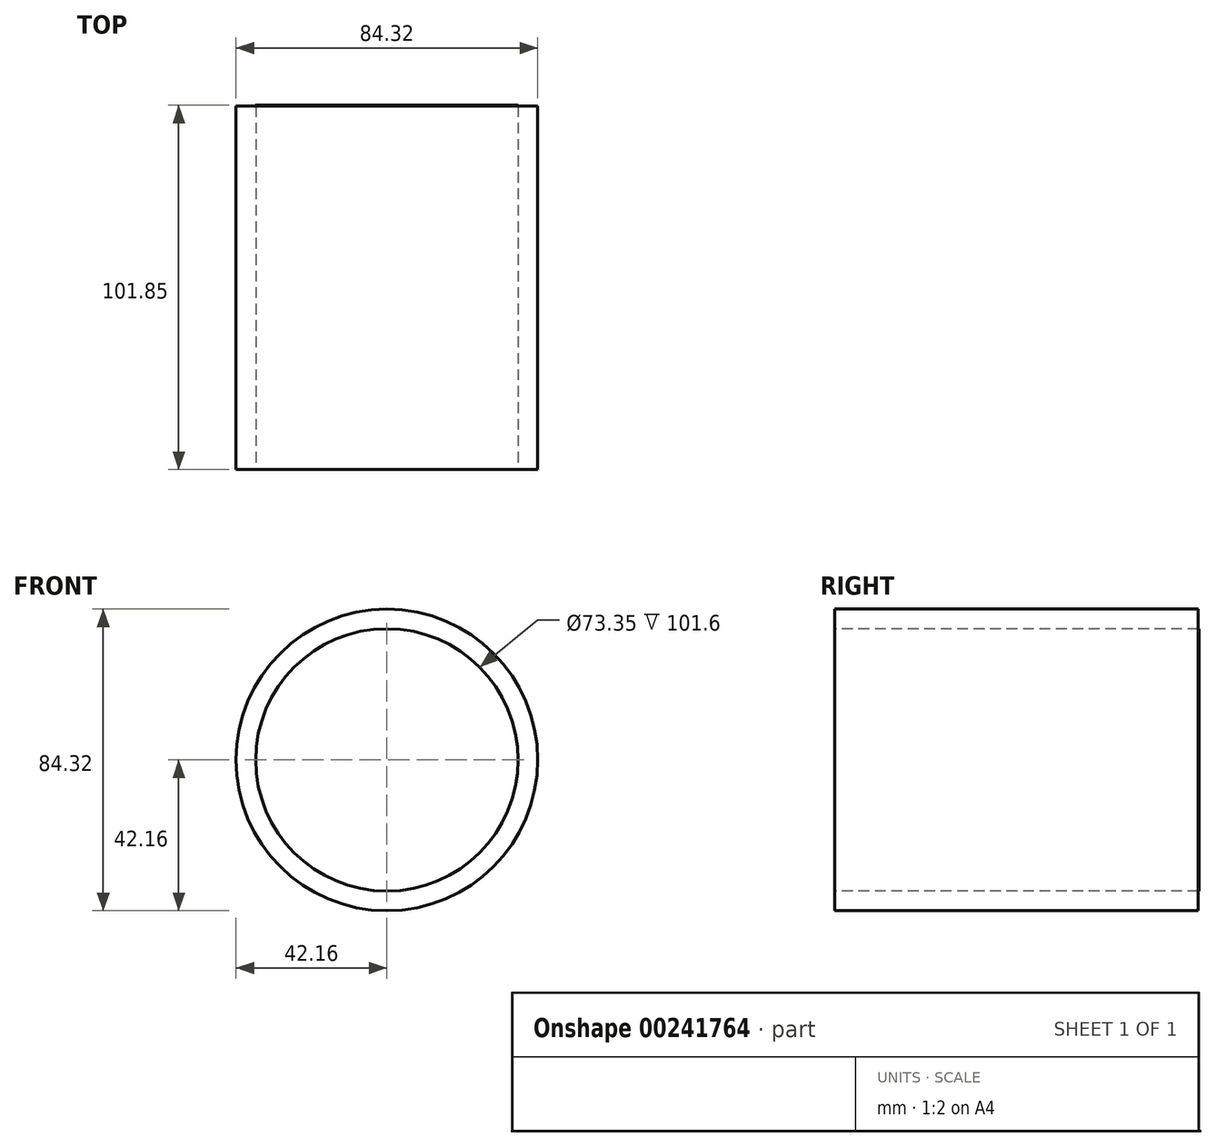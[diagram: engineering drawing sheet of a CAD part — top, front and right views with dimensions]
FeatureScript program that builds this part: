
annotation { "Feature Type Name" : "Feature", "Feature Type Description" : "" }
export const myFeature = defineFeature(function(context is Context, id is Id, definition is map)
    precondition{}
    {
        {
            var Q0;
            Q0=qCreatedBy(makeId("Front.planeOp"),FACE);
            var sketch = newSketch(context, id + "F0", { "sketchPlane" : qUnion([Q0])});
            skCircle(sketch, "E0", {"center": v(0, 0) * mm, "radius": 42.16 * mm});
            skCircle(sketch, "E1", {"center": v(0, 0) * mm, "radius": 36.67 * mm});
            skSolve(sketch);
        }
        {
            var Q0;
            Q0 = qSketchRegion(id + "F0", true);
            extrude(context, id + "F1", {"entities" : qUnion([Q0]), "oppositeDirection" : true, "depth" : 101.6 * mm});
        }
        {
            var Q0;
            Q0=makeQuery(id+"F1.opExtrude","CAP_FACE",FACE,{"disambiguationData":[OSD([sQuery(id+"F0.wireOp",EDGE,"E0"),sQuery(id+"F0.wireOp",EDGE,"E1")])],"isStart":false});
            var sketch = newSketch(context, id + "F2", { "sketchPlane" : qUnion([Q0])});
            skCircle(sketch, "E2", {"center": v(0, 0) * mm, "radius": 36.7 * mm});
            skSolve(sketch);
        }
        {
            var Q0;
            Q0 = qSketchRegion(id + "F2", true);
            extrude(context, id + "F3", {"entities" : qUnion([Q0]), "operationType" : NewBodyOperationType.ADD, "depth" : 0.25 * mm});
        }
        {
            var Q0;
            Q0=qCreatedBy(makeId("Right.planeOp"),FACE);
            var sketch = newSketch(context, id + "F4", { "sketchPlane" : qUnion([Q0])});
            skFitSpline(sketch, "E3", {"points": [v(2.39, -43.99) * mm, v(16.51, -67.5) * mm, v(52.53, -70.14) * mm, v(88.1, -66.72) * mm, v(94.18, -46.25) * mm], "startDerivative": vector(42.71, -120.41) * mm, "endDerivative": vector(6.17, 116.7) * mm});
            skFitSpline(sketch, "E4", {"points": [v(94.18, -46.25) * mm, v(94.18, -41.57) * mm], "startDerivative": vector(0, 4.69) * mm, "endDerivative": vector(0, 4.69) * mm});
            skFitSpline(sketch, "E5", {"points": [v(2.39, -43.99) * mm, v(2.39, -41.39) * mm], "startDerivative": vector(0, 2.6) * mm, "endDerivative": vector(0, 2.6) * mm});
            skFitSpline(sketch, "E6", {"points": [v(5.8, -43.99) * mm, v(18.26, -61.98) * mm, v(54.3, -63.38) * mm, v(81, -60.87) * mm, v(84.85, -53.6) * mm, v(85.79, -41.6) * mm], "startDerivative": vector(41.98, -104.35) * mm, "endDerivative": vector(3.32, 80.13) * mm});
            skSolve(sketch);
        }
        {
            var Q0;
            Q0=sQuery(id+"F4.wireOp",EDGE,"E3");
            var Q1;
            Q1=sQuery(id+"F4.wireOp",EDGE,"E6");
            var Q2;
            Q2=sQuery(id+"F4.wireOp",EDGE,"E4");
            extrude(context, id + "F5", {"bodyType" : ToolBodyType.SURFACE, "surfaceEntities" : qUnion([Q0, Q1, Q2]), "depth" : 25.4 * mm});
        }
    });
